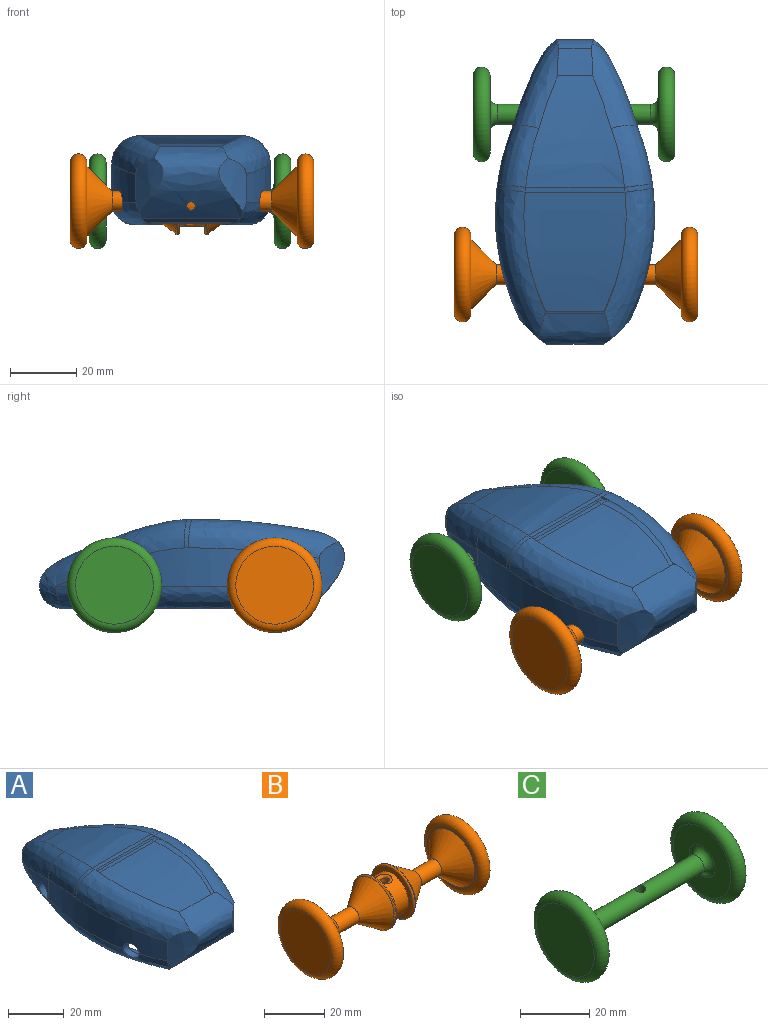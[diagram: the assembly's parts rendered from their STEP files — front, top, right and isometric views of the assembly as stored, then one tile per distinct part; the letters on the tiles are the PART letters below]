
ASSEMBLY  parts=3 mates=2
PART A: 72 faces, bbox 48.2x108.1x27.2 mm
  f0: cylinder r=4.31mm len=3.02mm, axis (-1,0,0), area 3.3mm2, adj f15,f18,f68
  f1: extruded ~57.81x11.53mm, area 602.9mm2, adj f2,f6,f19,f29,f30,f31,f32,f65
  f2: extruded ~21.91x8.99mm, area 77mm2, adj f1,f5,f32,f66
  f3: extruded ~21.91x8.99mm, area 77mm2, adj f4,f8,f25,f63
  f4: extruded ~57.81x11.53mm, area 602.8mm2, adj f3,f7,f24,f25,f26,f27,f28,f64
  f5: bspline ~28.87x16.61mm, area 234.5mm2, adj f2,f6,f33,f43,f66
  f6: bspline ~59.5x14.29mm, area 600.1mm2, adj f1,f5,f17,f19,f34,f42,f65
  f7: bspline ~66.73x17.58mm, area 600.1mm2, adj f4,f8,f17,f24,f34,f41,f64
  f8: bspline ~28.87x16.61mm, area 234.5mm2, adj f3,f7,f36,f40,f63
  f9: extruded ~55.6x11.53mm, area 579.3mm2, adj f10,f14,f44,f54,f55,f56,f57,f65
  f10: extruded ~21.44x8.78mm, area 75.8mm2, adj f9,f13,f57,f66
  f11: extruded ~21.44x8.78mm, area 75.8mm2, adj f12,f16,f50,f63
  f12: extruded ~55.6x11.53mm, area 579.3mm2, adj f11,f15,f49,f50,f51,f52,f53,f64
  f13: bspline ~22.85x12.51mm, area 138.7mm2, adj f10,f14,f43,f58,f66
  f14: bspline ~59.15x12.33mm, area 356.7mm2, adj f9,f13,f18,f42,f44,f59,f65
  f15: bspline ~56.23x11.14mm, area 356.7mm2, adj f0,f12,f16,f18,f41,f49,f64
  f16: bspline ~27.52x14.19mm, area 138.7mm2, adj f11,f15,f40,f61,f63
  f17: extruded ~31.13x21.58mm, area 657.2mm2, adj f6,f7,f19,f21,f24,f28,f29,f34
  f18: extruded ~28.3x17.28mm, area 466mm2, adj f0,f14,f15,f44,f46,f49,f53,f54
  f19: extruded ~15.79x8.27mm, area 108.2mm2, adj f1,f6,f17,f29
  f20: extruded ~30.11x1.44mm, area 43.2mm2, adj f21,f23,f27,f30
  f21: extruded ~36.72x30.99mm, area 1009.7mm2, adj f17,f20,f27,f28,f29,f30
  f22: extruded ~10.62x8.34mm, area 98.6mm2, adj f23,f25,f32,f35
  f23: extruded ~33.71x29.87mm, area 739.8mm2, adj f20,f22,f25,f26,f31,f32
  f24: extruded ~15.79x8.27mm, area 108.2mm2, adj f4,f7,f17,f28
  f25: bspline ~28.22x18.47mm, area 314.1mm2, adj f3,f4,f22,f23,f26,f35,f36
  f26: bspline ~20.51x12.56mm, area 245.3mm2, adj f4,f23,f25,f27
  f27: bspline ~8.72x8.62mm, area 18.9mm2, adj f4,f20,f21,f26,f28
  f28: bspline ~49.43x18.85mm, area 567.7mm2, adj f4,f17,f21,f24,f27
  f29: bspline ~59.45x22.19mm, area 567.7mm2, adj f1,f17,f19,f21,f30
  f30: bspline ~8.72x8.62mm, area 18.9mm2, adj f1,f20,f21,f29,f31
  f31: bspline ~20.51x12.56mm, area 245.3mm2, adj f1,f23,f30,f32
  f32: bspline ~28.22x18.47mm, area 314.1mm2, adj f1,f2,f22,f23,f31,f33,f35
  f33: bspline ~16.64x11.76mm, area 68.2mm2, adj f5,f32,f35,f37
  f34: cylinder r=6.85mm len=29.84mm, axis (-1,0,0), area 80.9mm2, adj f6,f7,f17,f67,f68,f69
  f35: cylinder r=6.85mm len=12.29mm, axis (-1,0,0), area 169.3mm2, adj f22,f25,f32,f33,f36,f38
  f36: bspline ~16.64x11.76mm, area 68.2mm2, adj f8,f25,f35,f39
  f37: bspline ~2.54x1.57mm, area 4.9mm2, adj f33,f38,f43,f58
  f38: plane 6.08x2.54mm, normal (0,-1,0), area 15.4mm2, adj f35,f37,f39,f60
  f39: bspline ~2.54x1.57mm, area 4.9mm2, adj f36,f38,f40,f61
  f40: bspline ~20.65x8.41mm, area 56.7mm2, adj f8,f16,f39,f41
  f41: bspline ~49.72x5.48mm, area 129.7mm2, adj f7,f15,f40,f68
  f42: bspline ~49.72x5.48mm, area 129.7mm2, adj f6,f14,f43,f67
  f43: bspline ~20.65x8.41mm, area 56.7mm2, adj f5,f13,f37,f42
  f44: extruded ~13.15x6.85mm, area 77.9mm2, adj f9,f14,f18,f54
  f45: extruded ~30.12x1.33mm, area 39.8mm2, adj f46,f48,f52,f55
  f46: extruded ~36.25x30.99mm, area 997.3mm2, adj f18,f45,f52,f53,f54,f55
  f47: extruded ~10.62x7.8mm, area 87.6mm2, adj f48,f50,f57,f60
  f48: extruded ~32.78x29.87mm, area 716.3mm2, adj f45,f47,f50,f51,f56,f57
  f49: extruded ~13.15x6.85mm, area 77.9mm2, adj f12,f15,f18,f53
  f50: bspline ~26.92x16.05mm, area 214.1mm2, adj f11,f12,f47,f48,f51,f60,f61
  f51: bspline ~19.11x10.06mm, area 165.6mm2, adj f12,f48,f50,f52
  f52: bspline ~6.2x6.07mm, area 12.4mm2, adj f12,f45,f46,f51,f53
  f53: bspline ~47.67x16.31mm, area 381.5mm2, adj f12,f18,f46,f49,f52
  f54: bspline ~57.58x19.65mm, area 381.5mm2, adj f9,f18,f44,f46,f55
  f55: bspline ~6.19x6.07mm, area 12.4mm2, adj f9,f45,f46,f54,f56
  f56: bspline ~19.11x10.06mm, area 165.6mm2, adj f9,f48,f55,f57
  f57: bspline ~26.92x16.05mm, area 214.1mm2, adj f9,f10,f47,f48,f56,f58,f60
  f58: bspline ~6.67x5.7mm, area 26mm2, adj f13,f37,f57,f60
  f59: cylinder r=4.31mm len=3.02mm, axis (-1,0,0), area 3.3mm2, adj f14,f18,f67
  f60: cylinder r=4.31mm len=9.53mm, axis (-1,0,0), area 92.8mm2, adj f38,f47,f50,f57,f58,f61
  f61: bspline ~10.66x7.17mm, area 26mm2, adj f16,f39,f50,f60
  f62: cylinder r=1.27mm len=5.18mm, axis (0,1,0), area 14.5mm2, adj f17,f71
  f63: cylinder r=3.17mm len=6.35mm, axis (-1,0,0), area 53.6mm2, adj f3,f8,f11,f16
  f64: cylinder r=3.17mm len=6.35mm, axis (-1,0,0), area 52.6mm2, adj f4,f7,f12,f15
  f65: cylinder r=3.17mm len=6.35mm, axis (-1,0,0), area 52.6mm2, adj f1,f6,f9,f14
  f66: cylinder r=3.17mm len=6.35mm, axis (-1,0,0), area 53.6mm2, adj f2,f5,f10,f13
  f67: plane 4.21x3.46mm, normal (-1,0,0), area 7.4mm2, adj f18,f34,f42,f59,f69,f70
  f68: plane 4.21x3.46mm, normal (1,0,0), area 7.4mm2, adj f0,f18,f34,f41,f69,f70
  f69: plane 23.62x0.02mm, normal (0,1,0), area 0.5mm2, adj f34,f67,f68,f70
  f70: cylinder r=7.94mm len=23.62mm, axis (-1,0,0), area 90.8mm2, adj f18,f67,f68,f69,f71
  f71: bspline ~5.31x4.98mm, area 24.9mm2, adj f18,f62,f70
PART B: 22 faces, bbox 73.7x31x31 mm
  f0: cylinder r=7.62mm len=15.24mm, axis (-1,0,0), area 319.1mm2, adj f1,f6,f14,f15
  f1: plane 18.97x18.97mm, normal (1,0,0), area 100.2mm2, adj f0,f12
  f2: plane 23.52x23.52mm, normal (-1,0,0), area 434.5mm2, adj f3
  f3: torus R=11.76mm, axis (1,0,0), area 670.7mm2, adj f2,f4
  f4: plane 23.52x23.52mm, normal (1,0,0), area 78.5mm2, adj f3,f21
  f5: cylinder r=3.02mm len=9.57mm, axis (-1,0,0), area 181.9mm2, adj f19,f21
  f6: plane 18.97x18.97mm, normal (-1,0,0), area 100.2mm2, adj f0,f11
  f7: plane 23.52x23.52mm, normal (1,0,0), area 434.5mm2, adj f8
  f8: torus R=11.76mm, axis (-1,0,0), area 670.7mm2, adj f7,f9
  f9: plane 23.52x23.52mm, normal (-1,0,0), area 78.5mm2, adj f8,f20
  f10: cylinder r=3.02mm len=9.57mm, axis (-1,0,0), area 181.9mm2, adj f18,f20
  f11: torus R=9.49mm, axis (1,0,0), area 66mm2, adj f6,f16
  f12: torus R=9.49mm, axis (-1,0,0), area 66mm2, adj f1,f17
  f13: cylinder r=1.59mm len=13.4mm, axis (0,0,1), area 128.9mm2, adj f14,f15
  f14: bspline ~5.71x5.02mm, area 20.4mm2, adj f0,f13
  f15: bspline ~5.71x5.02mm, area 20.4mm2, adj f0,f13
  f16: torus R=9.39mm, axis (-1,0,0), area 47.9mm2, adj f11,f18
  f17: torus R=9.39mm, axis (-1,0,0), area 47.9mm2, adj f12,f19
  f18: cone r=3.02mm half-angle=34.9deg, axis (-1,0,0), area 463.1mm2, adj f10,f16
  f19: cone r=9.66mm half-angle=34.9deg, axis (1,0,0), area 463.1mm2, adj f5,f17
  f20: cone r=10.64mm half-angle=45deg, axis (1,0,0), area 462.8mm2, adj f9,f10
  f21: cone r=3.02mm half-angle=45deg, axis (-1,0,0), area 462.8mm2, adj f4,f5
PART C: 10 faces, bbox 61x31x31 mm
  f0: plane 23.52x23.52mm, normal (-1,0,0), area 434.5mm2, adj f1
  f1: torus R=11.76mm, axis (1,0,0), area 670.7mm2, adj f0,f2
  f2: plane 23.52x23.52mm, normal (1,0,0), area 346.4mm2, adj f1,f3
  f3: torus R=5.29mm, axis (1,0,0), area 86.2mm2, adj f2,f8
  f4: plane 23.52x23.52mm, normal (1,0,0), area 434.5mm2, adj f5
  f5: torus R=11.76mm, axis (-1,0,0), area 670.7mm2, adj f4,f6
  f6: plane 23.52x23.52mm, normal (-1,0,0), area 346.4mm2, adj f5,f7
  f7: torus R=5.29mm, axis (-1,0,0), area 86.2mm2, adj f6,f8
  f8: cylinder r=3.02mm len=46.26mm, axis (-1,0,0), area 862.8mm2, adj f3,f7,f9
  f9: cylinder r=1.59mm len=6.05mm, axis (0,0,1), area 55.9mm2, adj f8
PLACE A t=(-22.51,-7.3,4.77)mm fixed
PLACE B rot(axis=(-1,0,0),25.6deg) t=(-59.05,-39.92,-7.2)mm
PLACE C rot(axis=(-1,0,0),154deg) t=(-53.3,8.51,-7.2)mm
MATE cylindrical C.f3 <-> A.f63  axis (-1,0,0) through (-45.95,8.51,-7.2)mm
MATE cylindrical A.f64 <-> B.f5  axis (-1,0,0) through (-42.61,-39.92,-7.2)mm
